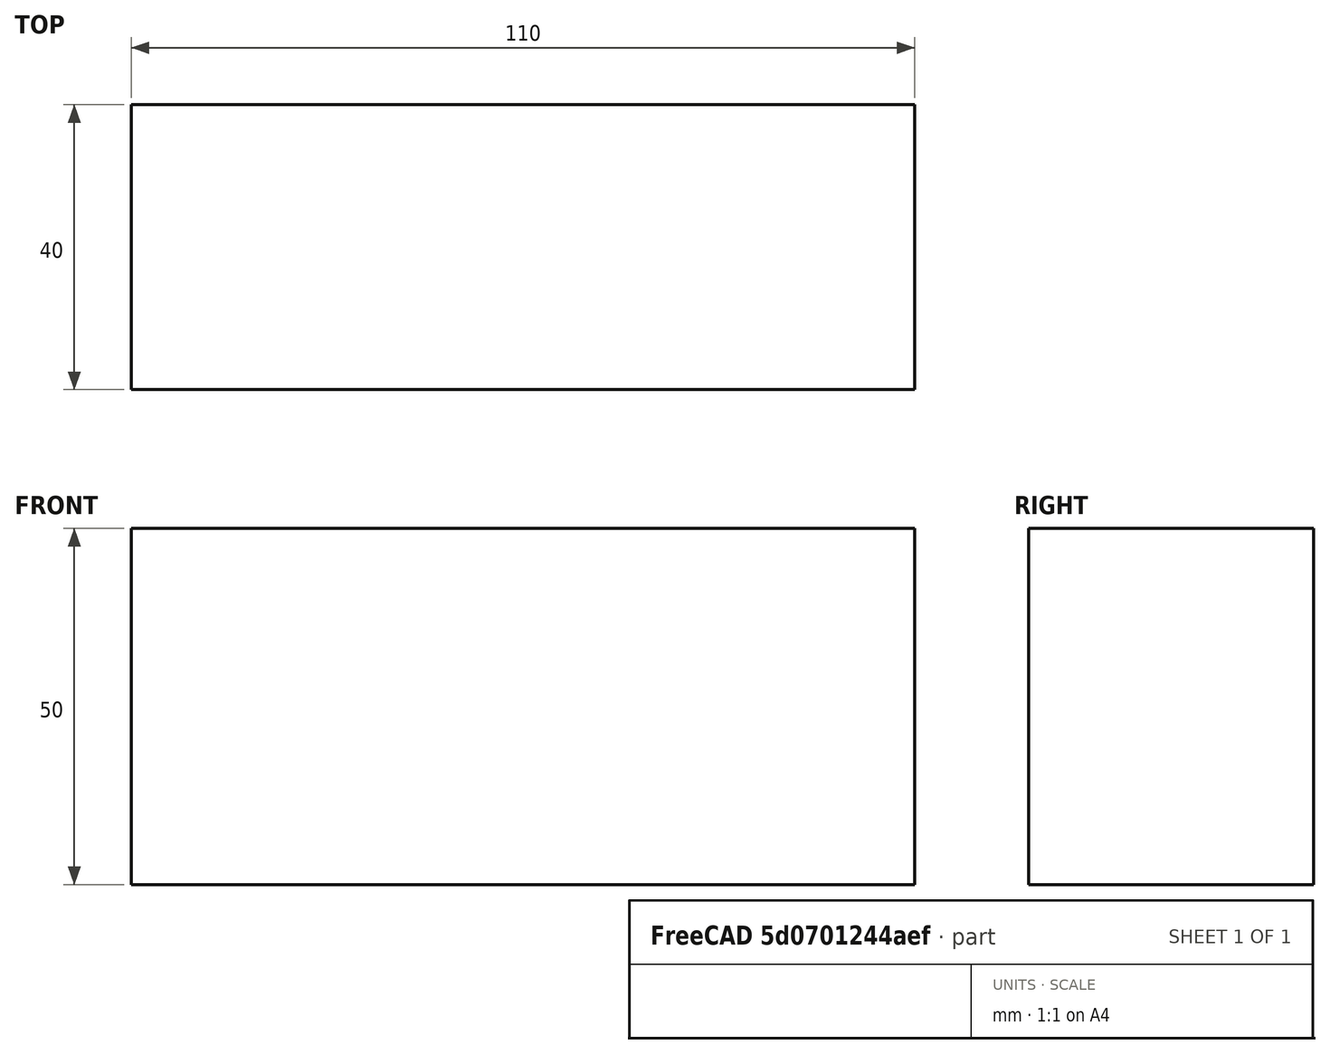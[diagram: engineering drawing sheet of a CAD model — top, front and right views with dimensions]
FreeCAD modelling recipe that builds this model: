
FCSTD DOCUMENT  (FreeCAD 0.15R4671 (Git))
Label: Flat Bar 110x40 EN10058 S235JR
License: All rights reserved
LicenseURL: http://en.wikipedia.org/wiki/All_rights_reserved
objects: Sketcher::SketchObject×1, Part::Extrusion×1
note: 2 computed .brp shape members not serialized (recipe doc carries the construction recipe); baked Part::Feature solids carry a one-line shape summary decoded from their .brp

FEATURE [Sketcher::SketchObject] Sketch
  sketch-geometry (4):
    g0: LineSegment StartX=-55 StartY=-20 StartZ=0 EndX=55 EndY=-20 EndZ=0
    g1: LineSegment StartX=55 StartY=-20 StartZ=0 EndX=55 EndY=20 EndZ=0
    g2: LineSegment StartX=55 StartY=20 StartZ=0 EndX=-55 EndY=20 EndZ=0
    g3: LineSegment StartX=-55 StartY=20 StartZ=0 EndX=-55 EndY=-20 EndZ=0
  constraints (12):
    c: Coincident(g0,g1)
    c: Coincident(g1,g2)
    c: Coincident(g2,g3)
    c: Coincident(g3,g0)
    c: Horizontal(g0)
    c: Horizontal(g2)
    c: Vertical(g1)
    c: Vertical(g3)
    c: Symmetric(g1,g2,g-2)
    c: Symmetric(g0,g1,g-1)
    c: DistanceY(g1) = 40
    c: DistanceX(g0) = 110
FEATURE [Part::Extrusion] Extrude  label="Flat Bar 110x40 EN10058 S235JR"
  Base = -> Sketch
  Dir = (0,0,50)
  Solid = true
